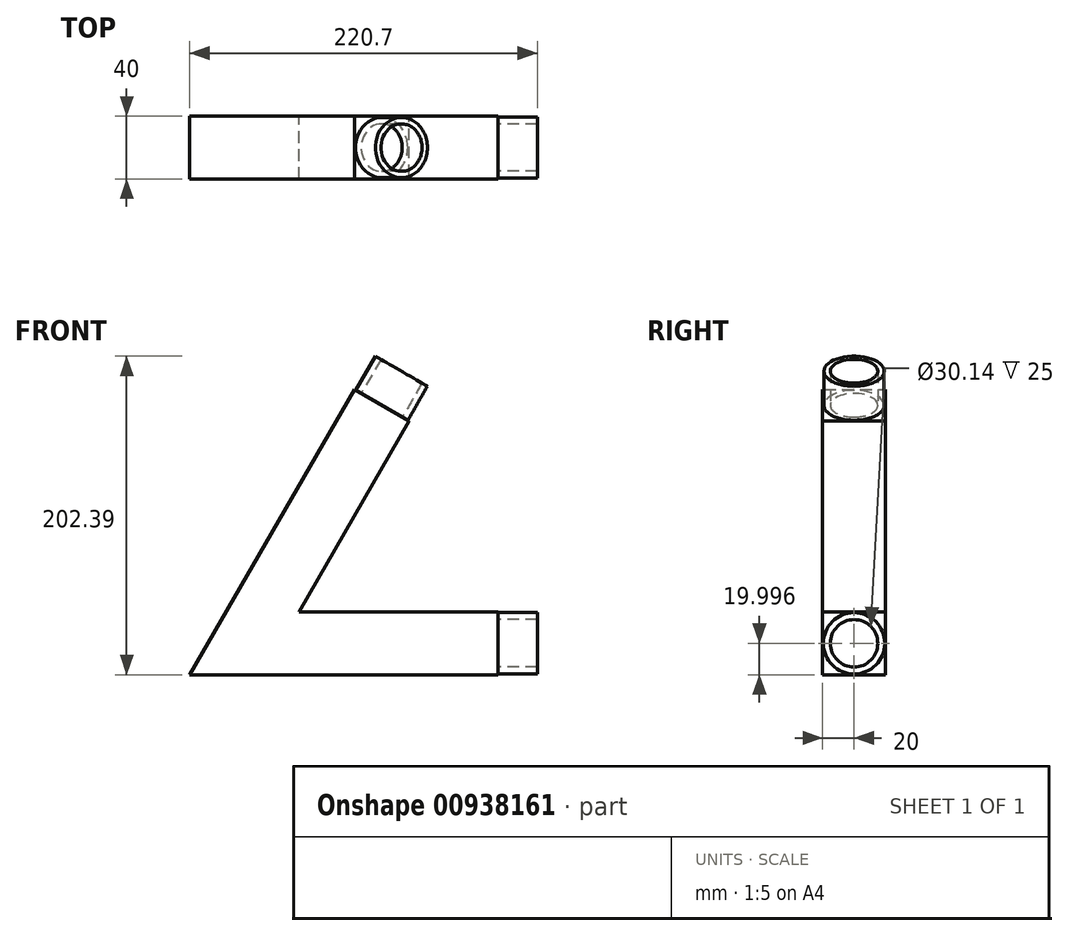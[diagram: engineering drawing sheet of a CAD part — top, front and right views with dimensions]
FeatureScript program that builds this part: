
annotation { "Feature Type Name" : "Feature", "Feature Type Description" : "" }
export const myFeature = defineFeature(function(context is Context, id is Id, definition is map)
    precondition{}
    {
        {
            var Q0;
            Q0=qCreatedBy(makeId("Front.planeOp"),FACE);
            var sketch = newSketch(context, id + "F0", { "sketchPlane" : qUnion([Q0])});
            skLineSegment(sketch, "E0", {"start": v(-65.38, -32.3) * mm, "end": v(61.04, -32.3) * mm});
            skLineSegment(sketch, "E1", {"start": v(-65.38, -32.3) * mm, "end": v(4.6, 88.9) * mm});
            skLineSegment(sketch, "E2", {"start": v(4.6, 88.9) * mm, "end": v(-30.05, 108.9) * mm});
            skLineSegment(sketch, "E3", {"start": v(-30.05, 108.9) * mm, "end": v(-134.66, -72.3) * mm});
            skLineSegment(sketch, "E4", {"start": v(61.04, -32.3) * mm, "end": v(61.04, -72.3) * mm});
            skLineSegment(sketch, "E5", {"start": v(61.04, -72.3) * mm, "end": v(-134.66, -72.3) * mm});
            skSolve(sketch);
        }
        {
            var Q0;
            Q0=makeQuery(id+"F0.imprint","IMPRINT",FACE,{"disambiguationData":[TD([[makeQuery(id+"F0.imprint","IMPRINT",EDGE,{"derivedFrom":sQuery(id+"F0.wireOp",EDGE,"E0")}),-1.0]])]});
            extrude(context, id + "F1", {"entities" : qUnion([Q0]), "depth" : 40 * mm, "offsetDistance" : 25 * mm});
        }
        {
            var Q0;
            Q0=makeQuery(id+"F1.opExtrude","SWEPT_FACE",FACE,{"disambiguationData":[OSD([sQuery(id+"F0.wireOp",EDGE,"E2")])]});
            var sketch = newSketch(context, id + "F2", { "sketchPlane" : qUnion([Q0])});
            skLineSegment(sketch, "E6", {"start": v(-80.47, -40) * mm, "end": v(-40.47, 0) * mm, "construction": true});
            skLineSegment(sketch, "E7", {"start": v(-40.47, 0) * mm, "end": v(-80.47, 0) * mm, "construction": true});
            skLineSegment(sketch, "E8", {"start": v(-80.47, 0) * mm, "end": v(-40.47, -40) * mm, "construction": true});
            skCircle(sketch, "E9", {"center": v(-60.47, -20) * mm, "radius": 15.07 * mm});
            skCircle(sketch, "E10", {"center": v(-60.47, -20) * mm, "radius": 19.1 * mm});
            skSolve(sketch);
        }
        {
            var Q0;
            Q0=makeQuery(id+"F2.imprint","IMPRINT",FACE,{"disambiguationData":[TD([[makeQuery(id+"F2.imprint","IMPRINT",EDGE,{"derivedFrom":sQuery(id+"F2.wireOp",EDGE,"E9")}),-1.0]])]});
            extrude(context, id + "F3", {"entities" : qUnion([Q0]), "operationType" : NewBodyOperationType.ADD, "depth" : 25 * mm, "offsetDistance" : 25 * mm});
        }
        {
            var Q0;
            Q0=makeQuery(id+"F1.opExtrude","SWEPT_FACE",FACE,{"disambiguationData":[OSD([sQuery(id+"F0.wireOp",EDGE,"E4")])]});
            var sketch = newSketch(context, id + "F4", { "sketchPlane" : qUnion([Q0])});
            skLineSegment(sketch, "E11", {"start": v(-40, -72.3) * mm, "end": v(0, -32.3) * mm, "construction": true});
            skLineSegment(sketch, "E12", {"start": v(0, -32.3) * mm, "end": v(-40, -32.3) * mm, "construction": true});
            skLineSegment(sketch, "E13", {"start": v(-40, -32.3) * mm, "end": v(0, -72.3) * mm, "construction": true});
            skCircle(sketch, "E14", {"center": v(-20, -52.3) * mm, "radius": 15.07 * mm});
            skCircle(sketch, "E15", {"center": v(-20, -52.3) * mm, "radius": 19.49 * mm});
            skSolve(sketch);
        }
        {
            var Q0;
            Q0=makeQuery(id+"F4.imprint","IMPRINT",FACE,{"disambiguationData":[TD([[makeQuery(id+"F4.imprint","IMPRINT",EDGE,{"derivedFrom":sQuery(id+"F4.wireOp",EDGE,"E14")}),-1.0]])]});
            extrude(context, id + "F5", {"entities" : qUnion([Q0]), "operationType" : NewBodyOperationType.ADD, "depth" : 25 * mm, "offsetDistance" : 25 * mm});
        }
    });
